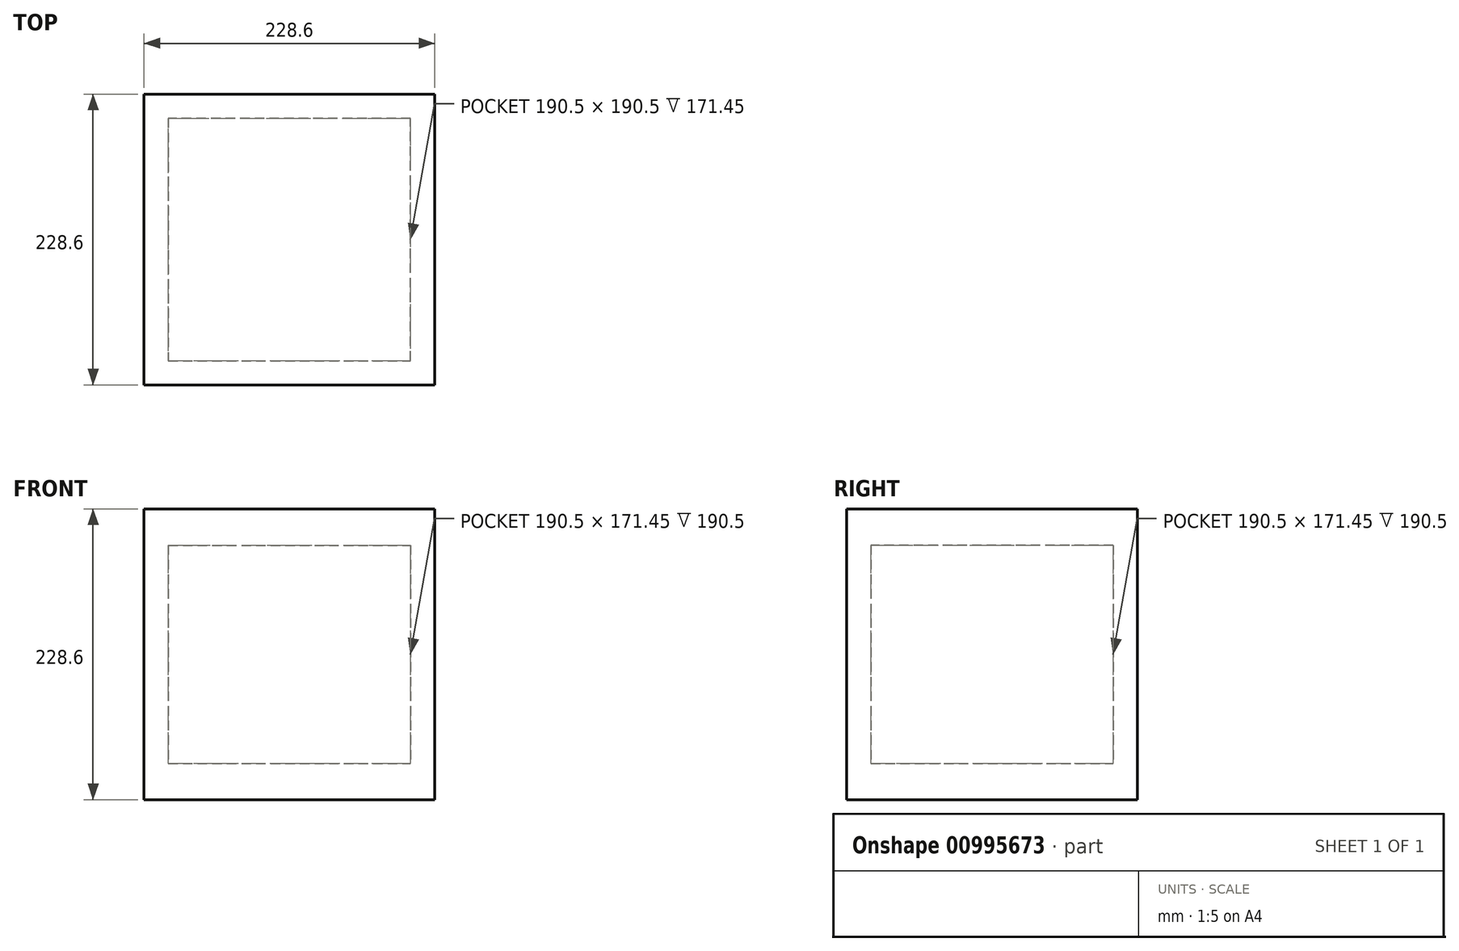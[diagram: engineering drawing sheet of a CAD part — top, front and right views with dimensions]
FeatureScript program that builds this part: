
annotation { "Feature Type Name" : "Feature", "Feature Type Description" : "" }
export const myFeature = defineFeature(function(context is Context, id is Id, definition is map)
    precondition{}
    {
        {
            var Q0;
            Q0=qCreatedBy(makeId("Top.planeOp"),FACE);
            var sketch = newSketch(context, id + "F0", { "sketchPlane" : qUnion([Q0])});
            skLineSegment(sketch, "E0.bottom", {"start": v(114.3, 114.3) * mm, "end": v(-114.3, 114.3) * mm});
            skLineSegment(sketch, "E0.top", {"start": v(114.3, -114.3) * mm, "end": v(-114.3, -114.3) * mm});
            skLineSegment(sketch, "E0.left", {"start": v(114.3, 114.3) * mm, "end": v(114.3, -114.3) * mm});
            skLineSegment(sketch, "E0.right", {"start": v(-114.3, 114.3) * mm, "end": v(-114.3, -114.3) * mm});
            skPoint(sketch, "E0.middle", {"position": v(0, 0) * mm});
            skSolve(sketch);
        }
        {
            var Q0;
            Q0=makeQuery(id+"F0.imprint","IMPRINT",FACE,{"disambiguationData":[TD([[makeQuery(id+"F0.imprint","IMPRINT",EDGE,{"derivedFrom":sQuery(id+"F0.wireOp",EDGE,"E0.bottom")}),1.0]])]});
            extrude(context, id + "F1", {"entities" : qUnion([Q0]), "depth" : 19.05 * mm, "offsetDistance" : 25.4 * mm});
        }
        {
            var Q0;
            Q0=makeQuery(id+"F1.opExtrude","CAP_FACE",FACE,{"disambiguationData":[OSD([sQuery(id+"F0.wireOp",EDGE,"E0.bottom"),sQuery(id+"F0.wireOp",EDGE,"E0.top"),sQuery(id+"F0.wireOp",EDGE,"E0.left"),sQuery(id+"F0.wireOp",EDGE,"E0.right")])],"isStart":false});
            var sketch = newSketch(context, id + "F2", { "sketchPlane" : qUnion([Q0])});
            skLineSegment(sketch, "E1.0.0", {"start": v(-114.3, -114.3) * mm, "end": v(114.3, -114.3) * mm});
            skLineSegment(sketch, "E1.0.1", {"start": v(114.3, -114.3) * mm, "end": v(114.3, 114.3) * mm});
            skLineSegment(sketch, "E1.0.2", {"start": v(114.3, 114.3) * mm, "end": v(-114.3, 114.3) * mm});
            skLineSegment(sketch, "E1.0.3", {"start": v(-114.3, 114.3) * mm, "end": v(-114.3, -114.3) * mm});
            skLineSegment(sketch, "E2.0", {"start": v(-95.25, 95.25) * mm, "end": v(-95.25, -95.25) * mm});
            skLineSegment(sketch, "E3.0", {"start": v(95.25, -95.25) * mm, "end": v(95.25, 95.25) * mm});
            skLineSegment(sketch, "E4.0", {"start": v(-95.25, -95.25) * mm, "end": v(95.25, -95.25) * mm});
            skLineSegment(sketch, "E5.0", {"start": v(95.25, 95.25) * mm, "end": v(-95.25, 95.25) * mm});
            skLineSegment(sketch, "E6.0", {"start": v(-95.25, -95.25) * mm, "end": v(-95.25, -114.3) * mm});
            skLineSegment(sketch, "E7.0", {"start": v(-95.25, 95.25) * mm, "end": v(-95.25, 114.3) * mm});
            skLineSegment(sketch, "E8", {"start": v(-95.25, -95.25) * mm, "end": v(-95.25, -95.25) * mm});
            skLineSegment(sketch, "E9", {"start": v(-95.25, 95.25) * mm, "end": v(-95.25, 95.25) * mm});
            skLineSegment(sketch, "E10.0", {"start": v(95.25, -95.25) * mm, "end": v(95.25, -114.3) * mm});
            skLineSegment(sketch, "E11.0", {"start": v(95.25, 95.25) * mm, "end": v(95.25, 114.3) * mm});
            skLineSegment(sketch, "E12", {"start": v(95.25, -95.25) * mm, "end": v(95.25, -95.25) * mm});
            skLineSegment(sketch, "E13", {"start": v(95.25, 95.25) * mm, "end": v(95.25, 95.25) * mm});
            skSolve(sketch);
        }
        {
            var Q0;
            {var subQ0=sQuery(id+"F2.wireOp",EDGE,"E1.0.3");Q0=makeQuery(id+"F2.imprint","IMPRINT",FACE,{"disambiguationData":[TD([[makeQuery(id+"F2.imprint","IMPRINT",EDGE,{"derivedFrom":subQ0}),1.0]])]});}
            extrude(context, id + "F3", {"entities" : qUnion([Q0]), "depth" : 190.5 * mm, "offsetDistance" : 25.4 * mm});
        }
        {
            var Q0;
            Q0=makeQuery(id+"F2.imprint","IMPRINT",FACE,{"disambiguationData":[TD([[makeQuery(id+"F2.imprint","IMPRINT",EDGE,{"derivedFrom":sQuery(id+"F2.wireOp",EDGE,"E5.0")}),-1.0]])]});
            extrude(context, id + "F4", {"entities" : qUnion([Q0]), "depth" : 190.5 * mm, "offsetDistance" : 25.4 * mm});
        }
        {
            var Q0;
            {var subQ1=sQuery(id+"F2.wireOp",EDGE,"E1.0.1");Q0=makeQuery(id+"F2.imprint","IMPRINT",FACE,{"disambiguationData":[TD([[makeQuery(id+"F2.imprint","IMPRINT",EDGE,{"derivedFrom":subQ1}),-1.0]])]});}
            extrude(context, id + "F5", {"entities" : qUnion([Q0]), "depth" : 190.5 * mm, "offsetDistance" : 25.4 * mm});
        }
        {
            var Q0;
            Q0=makeQuery(id+"F3.opExtrude","CAP_FACE",FACE,{"disambiguationData":[OSD([sQuery(id+"F2.wireOp",EDGE,"E1.0.0"),sQuery(id+"F2.wireOp",EDGE,"E1.0.2"),sQuery(id+"F2.wireOp",EDGE,"E1.0.3"),sQuery(id+"F2.wireOp",EDGE,"E2.0"),sQuery(id+"F2.wireOp",EDGE,"E6.0"),sQuery(id+"F2.wireOp",EDGE,"E7.0"),sQuery(id+"F2.wireOp",EDGE,"E8"),sQuery(id+"F2.wireOp",EDGE,"E9")])],"isStart":false});
            var sketch = newSketch(context, id + "F6", { "sketchPlane" : qUnion([Q0])});
            skLineSegment(sketch, "E14.bottom", {"start": v(-114.3, 114.3) * mm, "end": v(114.3, 114.3) * mm});
            skLineSegment(sketch, "E14.top", {"start": v(-114.3, -114.3) * mm, "end": v(114.3, -114.3) * mm});
            skLineSegment(sketch, "E14.left", {"start": v(-114.3, 114.3) * mm, "end": v(-114.3, -114.3) * mm});
            skLineSegment(sketch, "E14.right", {"start": v(114.3, 114.3) * mm, "end": v(114.3, -114.3) * mm});
            skLineSegment(sketch, "E15.bottom", {"start": v(-95.25, 95.25) * mm, "end": v(95.25, 95.25) * mm});
            skLineSegment(sketch, "E15.top", {"start": v(-95.25, -95.25) * mm, "end": v(95.25, -95.25) * mm});
            skLineSegment(sketch, "E15.left", {"start": v(-95.25, 95.25) * mm, "end": v(-95.25, -95.25) * mm});
            skLineSegment(sketch, "E15.right", {"start": v(95.25, 95.25) * mm, "end": v(95.25, -95.25) * mm});
            skSolve(sketch);
        }
        {
            var Q0;
            {var subQ1=sQuery(id+"F2.wireOp",EDGE,"E1.0.1");Q0=makeQuery(id+"F2.imprint","IMPRINT",FACE,{"disambiguationData":[TD([[makeQuery(id+"F2.imprint","IMPRINT",EDGE,{"derivedFrom":subQ1}),-1.0]])]});}
            extrude(context, id + "F7", {"entities" : qUnion([Q0]), "depth" : 190.5 * mm, "offsetDistance" : 25.4 * mm});
        }
        {
            var Q0;
            Q0=makeQuery(id+"F2.imprint","IMPRINT",FACE,{"disambiguationData":[TD([[makeQuery(id+"F2.imprint","IMPRINT",EDGE,{"derivedFrom":sQuery(id+"F2.wireOp",EDGE,"E4.0")}),-1.0]])]});
            extrude(context, id + "F8", {"entities" : qUnion([Q0]), "depth" : 190.5 * mm, "offsetDistance" : 25.4 * mm});
        }
        {
            var Q0;
            Q0=makeQuery(id+"F6.imprint","IMPRINT",FACE,{"disambiguationData":[TD([[makeQuery(id+"F6.imprint","IMPRINT",EDGE,{"derivedFrom":sQuery(id+"F6.wireOp",EDGE,"E15.bottom")}),-1.0]])]});
            extrude(context, id + "F9", {"entities" : qUnion([Q0]), "oppositeDirection" : true, "depth" : 9.52 * mm, "offsetDistance" : 25.4 * mm});
        }
        {
            var Q0;
            Q0=makeQuery(id+"F9.opExtrude","CAP_FACE",FACE,{"disambiguationData":[OSD([sQuery(id+"F6.wireOp",EDGE,"E15.bottom"),sQuery(id+"F6.wireOp",EDGE,"E15.top"),sQuery(id+"F6.wireOp",EDGE,"E15.left"),sQuery(id+"F6.wireOp",EDGE,"E15.right")])],"isStart":true});
            var Q1;
            Q1=makeQuery(id+"F3.opExtrude","CAP_FACE",FACE,{"disambiguationData":[OSD([sQuery(id+"F2.wireOp",EDGE,"E1.0.0"),sQuery(id+"F2.wireOp",EDGE,"E1.0.2"),sQuery(id+"F2.wireOp",EDGE,"E1.0.3"),sQuery(id+"F2.wireOp",EDGE,"E2.0"),sQuery(id+"F2.wireOp",EDGE,"E6.0"),sQuery(id+"F2.wireOp",EDGE,"E7.0"),sQuery(id+"F2.wireOp",EDGE,"E8"),sQuery(id+"F2.wireOp",EDGE,"E9")])],"isStart":false});
            var Q2;
            Q2=makeQuery(id+"F4.opExtrude","CAP_FACE",FACE,{"disambiguationData":[OSD([sQuery(id+"F2.wireOp",EDGE,"E1.0.2"),sQuery(id+"F2.wireOp",EDGE,"E5.0"),sQuery(id+"F2.wireOp",EDGE,"E7.0"),sQuery(id+"F2.wireOp",EDGE,"E9"),sQuery(id+"F2.wireOp",EDGE,"E11.0"),sQuery(id+"F2.wireOp",EDGE,"E13")])],"isStart":false});
            var Q3;
            Q3=makeQuery(id+"F8.opExtrude","CAP_FACE",FACE,{"disambiguationData":[OSD([sQuery(id+"F2.wireOp",EDGE,"E1.0.0"),sQuery(id+"F2.wireOp",EDGE,"E4.0"),sQuery(id+"F2.wireOp",EDGE,"E6.0"),sQuery(id+"F2.wireOp",EDGE,"E8"),sQuery(id+"F2.wireOp",EDGE,"E10.0"),sQuery(id+"F2.wireOp",EDGE,"E12")])],"isStart":false});
            var Q4;
            Q4=makeQuery(id+"F7.opExtrude","CAP_FACE",FACE,{"disambiguationData":[OSD([sQuery(id+"F2.wireOp",EDGE,"E1.0.0"),sQuery(id+"F2.wireOp",EDGE,"E1.0.1"),sQuery(id+"F2.wireOp",EDGE,"E1.0.2"),sQuery(id+"F2.wireOp",EDGE,"E3.0"),sQuery(id+"F2.wireOp",EDGE,"E10.0"),sQuery(id+"F2.wireOp",EDGE,"E11.0"),sQuery(id+"F2.wireOp",EDGE,"E12"),sQuery(id+"F2.wireOp",EDGE,"E13")])],"isStart":false});
            extrude(context, id + "F10", {"entities" : qUnion([Q0, Q1, Q2, Q3, Q4]), "operationType" : NewBodyOperationType.ADD, "depth" : 19.05 * mm, "offsetDistance" : 25.4 * mm});
        }
        {
            var Q0;
            Q0=makeQuery(id+"F2.imprint","IMPRINT",FACE,{"disambiguationData":[TD([[makeQuery(id+"F2.imprint","IMPRINT",EDGE,{"derivedFrom":sQuery(id+"F2.wireOp",EDGE,"E2.0")}),1.0]])]});
            extrude(context, id + "F11", {"entities" : qUnion([Q0]), "operationType" : NewBodyOperationType.ADD, "depth" : 9.52 * mm, "offsetDistance" : 25.4 * mm});
        }
    });
